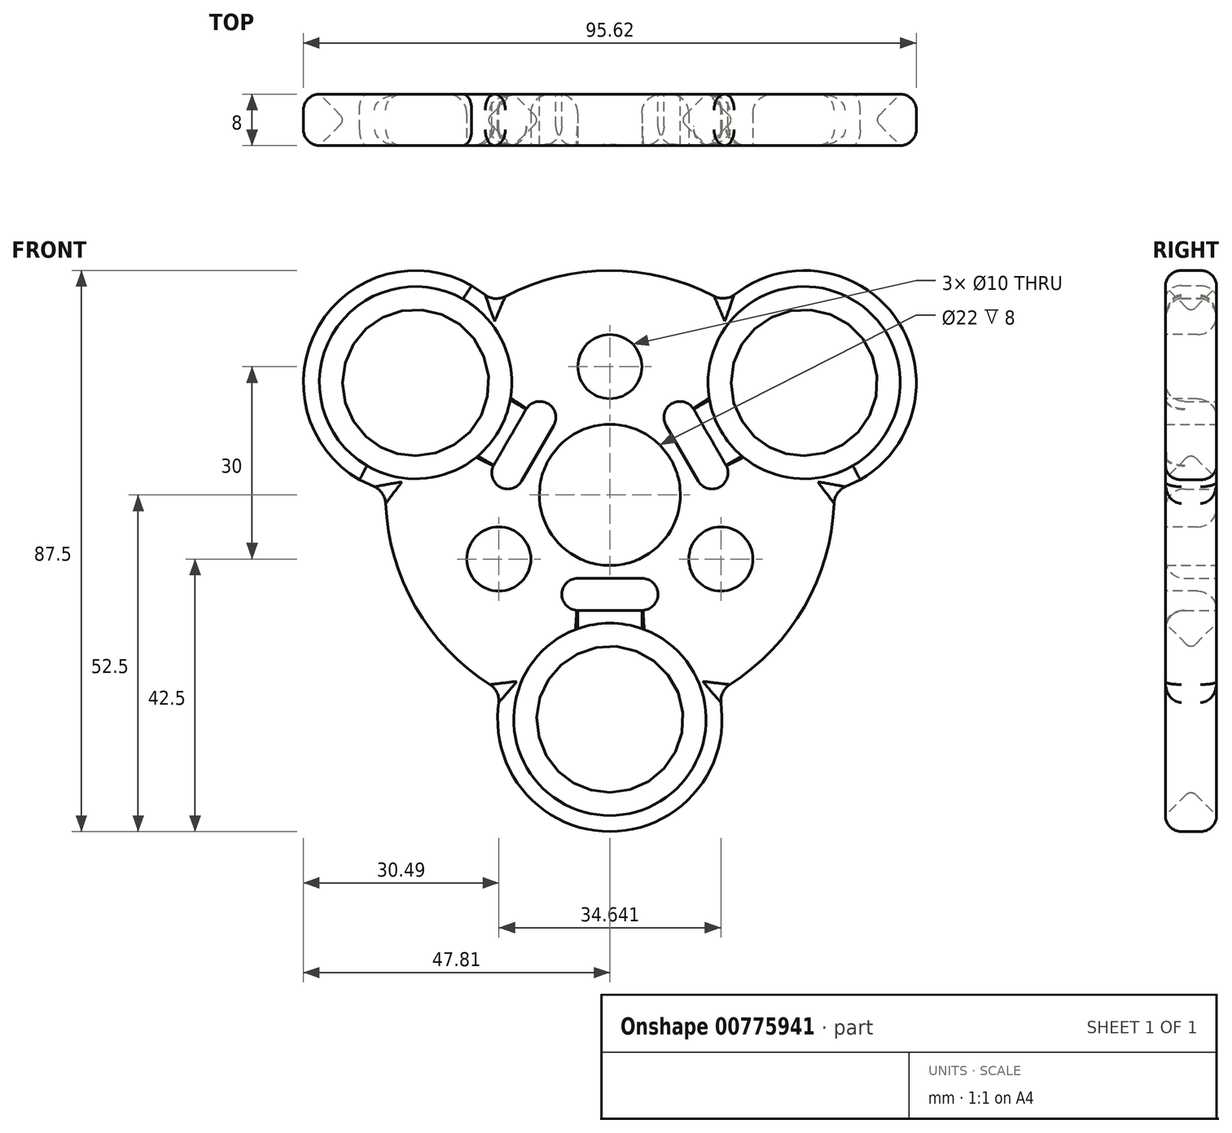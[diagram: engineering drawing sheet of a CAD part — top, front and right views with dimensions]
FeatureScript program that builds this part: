
annotation { "Feature Type Name" : "Feature", "Feature Type Description" : "" }
export const myFeature = defineFeature(function(context is Context, id is Id, definition is map)
    precondition{}
    {
        {
            var Q0;
            Q0=qCreatedBy(makeId("Front.planeOp"),FACE);
            var sketch = newSketch(context, id + "F0", { "sketchPlane" : qUnion([Q0])});
            skCircle(sketch, "E0", {"center": v(0, 0) * mm, "radius": 11 * mm});
            skCircle(sketch, "E1", {"center": v(0, 0) * mm, "radius": 17.5 * mm, "construction": true});
            skLineSegment(sketch, "E2", {"start": v(0, 0) * mm, "end": v(-30.31, 17.5) * mm, "construction": true});
            skLineSegment(sketch, "E3", {"start": v(0, 0) * mm, "end": v(30.31, 17.5) * mm, "construction": true});
            skLineSegment(sketch, "E4", {"start": v(0, 0) * mm, "end": v(0, -35) * mm, "construction": true});
            skCircle(sketch, "E5", {"center": v(-30.31, 17.5) * mm, "radius": 11 * mm});
            skCircle(sketch, "E6", {"center": v(30.31, 17.5) * mm, "radius": 11 * mm});
            skCircle(sketch, "E7", {"center": v(0, -35) * mm, "radius": 11 * mm});
            skArc(sketch, "E8", {"start": v(-19.01, 30.86) * mm, "mid": v(-45.47, 26.25) * mm, "end": v(-36.24, 1.03) * mm});
            skArc(sketch, "E9", {"start": v(36.2, 1.02) * mm, "mid": v(45.84, 25.57) * mm, "end": v(20.2, 31.79) * mm});
            skArc(sketch, "E10", {"start": v(-17.43, -33.4) * mm, "mid": v(0.01, -52.5) * mm, "end": v(17.42, -33.37) * mm});
            skLineSegment(sketch, "E11", {"start": v(-15.16, 8.75) * mm, "end": v(15.16, 8.75) * mm, "construction": true});
            skLineSegment(sketch, "E12", {"start": v(15.16, 8.75) * mm, "end": v(0, -17.5) * mm, "construction": true});
            skLineSegment(sketch, "E13", {"start": v(0, -17.5) * mm, "end": v(-15.16, 8.75) * mm, "construction": true});
            skLineSegment(sketch, "E14", {"start": v(0, 8.75) * mm, "end": v(0, 27.78) * mm, "construction": true});
            skLineSegment(sketch, "E15", {"start": v(7.58, -4.38) * mm, "end": v(29.6, -17.1) * mm, "construction": true});
            skLineSegment(sketch, "E16", {"start": v(-7.58, -4.37) * mm, "end": v(-25.82, -14.9) * mm, "construction": true});
            skLineSegment(sketch, "E17", {"start": v(-43.22, -4.87) * mm, "end": v(-17.4, 39.87) * mm, "construction": true});
            skLineSegment(sketch, "E18", {"start": v(12.19, 48.9) * mm, "end": v(48.44, -13.9) * mm, "construction": true});
            skLineSegment(sketch, "E19", {"start": v(-41.25, -35) * mm, "end": v(41.25, -35) * mm, "construction": true});
            skLineSegment(sketch, "E20", {"start": v(-21.56, 32.66) * mm, "end": v(0, 17.5) * mm});
            skLineSegment(sketch, "E21", {"start": v(0, 17.5) * mm, "end": v(21.52, 32.72) * mm});
            skLineSegment(sketch, "E22", {"start": v(-39.06, 2.34) * mm, "end": v(-15.16, -8.75) * mm});
            skLineSegment(sketch, "E23", {"start": v(-15.16, -8.75) * mm, "end": v(-17.57, -35) * mm});
            skLineSegment(sketch, "E24", {"start": v(39.06, 2.34) * mm, "end": v(15.12, -8.73) * mm});
            skLineSegment(sketch, "E25", {"start": v(15.12, -8.73) * mm, "end": v(17.58, -35) * mm});
            skSolve(sketch);
        }
        {
            var Q0;
            Q0=makeQuery(id+"F0.imprint","IMPRINT",FACE,{"disambiguationData":[TD([[makeQuery(id+"F0.imprint","IMPRINT",EDGE,{"derivedFrom":sQuery(id+"F0.wireOp",EDGE,"E0")}),-1.0]])]});
            extrude(context, id + "F1", {"entities" : qUnion([Q0]), "depth" : 8 * mm, "offsetDistance" : 25 * mm});
        }
        {
            var Q0;
            Q0=makeQuery(id+"F1.opExtrude","SWEPT_EDGE",EDGE,{"disambiguationData":[OSD([sQuery(id+"F0.wireOp",EDGE,"E24"),sQuery(id+"F0.wireOp",EDGE,"E25")])]});
            var Q1;
            Q1=makeQuery(id+"F1.opExtrude","SWEPT_EDGE",EDGE,{"disambiguationData":[OSD([sQuery(id+"F0.wireOp",EDGE,"E22"),sQuery(id+"F0.wireOp",EDGE,"E23")])]});
            var Q2;
            Q2=makeQuery(id+"F1.opExtrude","SWEPT_EDGE",EDGE,{"disambiguationData":[OSD([sQuery(id+"F0.wireOp",EDGE,"E20"),sQuery(id+"F0.wireOp",EDGE,"E21")])]});
            fillet(context, id + "F2", {"entities" : qUnion([Q0, Q1, Q2]), "radius" : 10 * mm, "tangentPropagation" : true, "allowEdgeOverflow" : false});
        }
        {
            var Q0;
            Q0=qCreatedBy(makeId("Front.planeOp"),FACE);
            var sketch = newSketch(context, id + "F3", { "sketchPlane" : qUnion([Q0])});
            skArc(sketch, "E26", {"start": v(10.86, -33.27) * mm, "mid": v(30.31, -17.5) * mm, "end": v(34.25, 7.23) * mm});
            skCircle(sketch, "E27.0", {"center": v(0, 0) * mm, "radius": 11 * mm});
            skCircle(sketch, "E28.0", {"center": v(30.31, 17.5) * mm, "radius": 11 * mm});
            skCircle(sketch, "E29.0", {"center": v(-30.31, 17.5) * mm, "radius": 11 * mm});
            skCircle(sketch, "E30.0", {"center": v(0, -35) * mm, "radius": 11 * mm});
            skArc(sketch, "E31.trimOffspring", {"start": v(23.38, 26.04) * mm, "mid": v(0, 35) * mm, "end": v(-23.38, 26.04) * mm});
            skArc(sketch, "E32.trimOffspring", {"start": v(-34.25, 7.23) * mm, "mid": v(-30.31, -17.5) * mm, "end": v(-10.86, -33.27) * mm});
            skSolve(sketch);
        }
        {
            var Q0;
            {var subQ1=sQuery(id+"F3.wireOp",EDGE,"E26");Q0=makeQuery(id+"F3.imprint","IMPRINT",FACE,{"disambiguationData":[TD([[makeQuery(id+"F3.imprint","IMPRINT",EDGE,{"derivedFrom":subQ1}),1.0]])]});}
            var Q1;
            Q1=makeQuery(id+"F1.opExtrude","CAP_FACE",FACE,{"disambiguationData":[OSD([sQuery(id+"F0.wireOp",EDGE,"E0"),sQuery(id+"F0.wireOp",EDGE,"E5"),sQuery(id+"F0.wireOp",EDGE,"E6"),sQuery(id+"F0.wireOp",EDGE,"E7"),sQuery(id+"F0.wireOp",EDGE,"E8"),sQuery(id+"F0.wireOp",EDGE,"E9"),sQuery(id+"F0.wireOp",EDGE,"E10"),sQuery(id+"F0.wireOp",EDGE,"E20"),sQuery(id+"F0.wireOp",EDGE,"E21"),sQuery(id+"F0.wireOp",EDGE,"E22"),sQuery(id+"F0.wireOp",EDGE,"E23"),sQuery(id+"F0.wireOp",EDGE,"E24"),sQuery(id+"F0.wireOp",EDGE,"E25")])],"isStart":false});
            extrude(context, id + "F4", {"entities" : qUnion([Q0]), "operationType" : NewBodyOperationType.ADD, "endBound" : BoundingType.UP_TO_SURFACE, "depth" : 7 * mm, "endBoundEntityFace" : qUnion([Q1]), "offsetDistance" : 25 * mm});
        }
        {
            var Q0;
            Q0=makeQuery(id+"F4.opExtrude","CAP_EDGE",EDGE,{"disambiguationData":[OSD([sQuery(id+"F3.wireOp",EDGE,"E32.trimOffspring")])],"isStart":false});
            var Q1;
            Q1=makeQuery(id+"F1.opExtrude","CAP_EDGE",EDGE,{"disambiguationData":[OSD([sQuery(id+"F0.wireOp",EDGE,"E10")])],"isStart":false});
            var Q2;
            Q2=makeQuery(id+"F4.opExtrude","CAP_EDGE",EDGE,{"disambiguationData":[OSD([sQuery(id+"F3.wireOp",EDGE,"E26")])],"isStart":false});
            var Q3;
            Q3=makeQuery(id+"F1.opExtrude","CAP_EDGE",EDGE,{"disambiguationData":[OSD([sQuery(id+"F0.wireOp",EDGE,"E9")])],"isStart":false});
            var Q4;
            Q4=makeQuery(id+"F4.opExtrude","CAP_EDGE",EDGE,{"disambiguationData":[OSD([sQuery(id+"F3.wireOp",EDGE,"E31.trimOffspring")])],"isStart":false});
            var Q5;
            Q5=makeQuery(id+"F1.opExtrude","CAP_EDGE",EDGE,{"disambiguationData":[OSD([sQuery(id+"F0.wireOp",EDGE,"E8")])],"isStart":false});
            var Q6;
            Q6=makeQuery(id+"F1.opExtrude","CAP_EDGE",EDGE,{"disambiguationData":[OSD([sQuery(id+"F0.wireOp",EDGE,"E20")])],"isStart":false});
            var Q7;
            Q7=makeQuery(id+"F1.opExtrude","CAP_EDGE",EDGE,{"disambiguationData":[OSD([sQuery(id+"F0.wireOp",EDGE,"E22")])],"isStart":false});
            var Q8;
            Q8=makeQuery(id+"F1.opExtrude","CAP_EDGE",EDGE,{"disambiguationData":[OSD([sQuery(id+"F0.wireOp",EDGE,"E21")])],"isStart":false});
            var Q9;
            Q9=makeQuery(id+"F1.opExtrude","CAP_EDGE",EDGE,{"disambiguationData":[OSD([sQuery(id+"F0.wireOp",EDGE,"E24")])],"isStart":false});
            var Q10;
            Q10=makeQuery(id+"F4.opExtrude","CAP_EDGE",EDGE,{"disambiguationData":[OSD([sQuery(id+"F3.wireOp",EDGE,"E32.trimOffspring")])],"isStart":true});
            var Q11;
            Q11=makeQuery(id+"F1.opExtrude","CAP_EDGE",EDGE,{"disambiguationData":[OSD([sQuery(id+"F0.wireOp",EDGE,"E10")])],"isStart":true});
            var Q12;
            Q12=makeQuery(id+"F1.opExtrude","CAP_EDGE",EDGE,{"disambiguationData":[OSD([sQuery(id+"F0.wireOp",EDGE,"E23")])],"isStart":true});
            var Q13;
            Q13=makeQuery(id+"F1.opExtrude","CAP_EDGE",EDGE,{"disambiguationData":[OSD([sQuery(id+"F0.wireOp",EDGE,"E25")])],"isStart":true});
            var Q14;
            Q14=makeQuery(id+"F4.opExtrude","CAP_EDGE",EDGE,{"disambiguationData":[OSD([sQuery(id+"F3.wireOp",EDGE,"E26")])],"isStart":true});
            var Q15;
            Q15=makeQuery(id+"F1.opExtrude","CAP_EDGE",EDGE,{"disambiguationData":[OSD([sQuery(id+"F0.wireOp",EDGE,"E24")])],"isStart":true});
            var Q16;
            Q16=makeQuery(id+"F1.opExtrude","CAP_EDGE",EDGE,{"disambiguationData":[OSD([sQuery(id+"F0.wireOp",EDGE,"E9")])],"isStart":true});
            var Q17;
            Q17=makeQuery(id+"F1.opExtrude","CAP_EDGE",EDGE,{"disambiguationData":[OSD([sQuery(id+"F0.wireOp",EDGE,"E21")])],"isStart":true});
            var Q18;
            Q18=makeQuery(id+"F4.opExtrude","CAP_EDGE",EDGE,{"disambiguationData":[OSD([sQuery(id+"F3.wireOp",EDGE,"E31.trimOffspring")])],"isStart":true});
            var Q19;
            Q19=makeQuery(id+"F1.opExtrude","CAP_EDGE",EDGE,{"disambiguationData":[OSD([sQuery(id+"F0.wireOp",EDGE,"E20")])],"isStart":true});
            var Q20;
            Q20=makeQuery(id+"F1.opExtrude","CAP_EDGE",EDGE,{"disambiguationData":[OSD([sQuery(id+"F0.wireOp",EDGE,"E8")])],"isStart":true});
            var Q21;
            Q21=makeQuery(id+"F1.opExtrude","CAP_EDGE",EDGE,{"disambiguationData":[OSD([sQuery(id+"F0.wireOp",EDGE,"E22")])],"isStart":true});
            var Q22;
            Q22=makeQuery(id+"F4.opExtrude","TWEAK_EDGE",EDGE,{"derivedFrom":[makeQuery(id+"F1.opExtrude","CAP_FACE",FACE,{"disambiguationData":[OSD([sQuery(id+"F0.wireOp",EDGE,"E0"),sQuery(id+"F0.wireOp",EDGE,"E5"),sQuery(id+"F0.wireOp",EDGE,"E6"),sQuery(id+"F0.wireOp",EDGE,"E7"),sQuery(id+"F0.wireOp",EDGE,"E8"),sQuery(id+"F0.wireOp",EDGE,"E9"),sQuery(id+"F0.wireOp",EDGE,"E10"),sQuery(id+"F0.wireOp",EDGE,"E20"),sQuery(id+"F0.wireOp",EDGE,"E21"),sQuery(id+"F0.wireOp",EDGE,"E22"),sQuery(id+"F0.wireOp",EDGE,"E23"),sQuery(id+"F0.wireOp",EDGE,"E24"),sQuery(id+"F0.wireOp",EDGE,"E25")])],"isStart":false}),makeQuery(id+"F3.imprint","IMPRINT",EDGE,{"derivedFrom":sQuery(id+"F3.wireOp",EDGE,"E32.trimOffspring")})]});
            var Q23;
            Q23=makeQuery(id+"F4.opExtrude","TWEAK_EDGE",EDGE,{"derivedFrom":[makeQuery(id+"F1.opExtrude","CAP_FACE",FACE,{"disambiguationData":[OSD([sQuery(id+"F0.wireOp",EDGE,"E0"),sQuery(id+"F0.wireOp",EDGE,"E5"),sQuery(id+"F0.wireOp",EDGE,"E6"),sQuery(id+"F0.wireOp",EDGE,"E7"),sQuery(id+"F0.wireOp",EDGE,"E8"),sQuery(id+"F0.wireOp",EDGE,"E9"),sQuery(id+"F0.wireOp",EDGE,"E10"),sQuery(id+"F0.wireOp",EDGE,"E20"),sQuery(id+"F0.wireOp",EDGE,"E21"),sQuery(id+"F0.wireOp",EDGE,"E22"),sQuery(id+"F0.wireOp",EDGE,"E23"),sQuery(id+"F0.wireOp",EDGE,"E24"),sQuery(id+"F0.wireOp",EDGE,"E25")])],"isStart":false}),makeQuery(id+"F3.imprint","IMPRINT",EDGE,{"derivedFrom":sQuery(id+"F3.wireOp",EDGE,"E31.trimOffspring")})]});
            var Q24;
            Q24=makeQuery(id+"F4.opExtrude","TWEAK_EDGE",EDGE,{"derivedFrom":[makeQuery(id+"F1.opExtrude","CAP_FACE",FACE,{"disambiguationData":[OSD([sQuery(id+"F0.wireOp",EDGE,"E0"),sQuery(id+"F0.wireOp",EDGE,"E5"),sQuery(id+"F0.wireOp",EDGE,"E6"),sQuery(id+"F0.wireOp",EDGE,"E7"),sQuery(id+"F0.wireOp",EDGE,"E8"),sQuery(id+"F0.wireOp",EDGE,"E9"),sQuery(id+"F0.wireOp",EDGE,"E10"),sQuery(id+"F0.wireOp",EDGE,"E20"),sQuery(id+"F0.wireOp",EDGE,"E21"),sQuery(id+"F0.wireOp",EDGE,"E22"),sQuery(id+"F0.wireOp",EDGE,"E23"),sQuery(id+"F0.wireOp",EDGE,"E24"),sQuery(id+"F0.wireOp",EDGE,"E25")])],"isStart":false}),makeQuery(id+"F3.imprint","IMPRINT",EDGE,{"derivedFrom":sQuery(id+"F3.wireOp",EDGE,"E26")})]});
            var Q25;
            Q25=makeQuery(id+"F1.opExtrude","CAP_EDGE",EDGE,{"disambiguationData":[OSD([sQuery(id+"F0.wireOp",EDGE,"E25")])],"isStart":false});
            var Q26;
            Q26=makeQuery(id+"F1.opExtrude","CAP_EDGE",EDGE,{"disambiguationData":[OSD([sQuery(id+"F0.wireOp",EDGE,"E23")])],"isStart":false});
            fillet(context, id + "F5", {"entities" : qUnion([Q0, Q1, Q2, Q3, Q4, Q5, Q6, Q7, Q8, Q9, Q10, Q11, Q12, Q13, Q14, Q15, Q16, Q17, Q18, Q19, Q20, Q21, Q22, Q23, Q24, Q25, Q26]), "radius" : 2.5 * mm, "tangentPropagation" : true, "allowEdgeOverflow" : false});
        }
        {
            var Q0;
            Q0=makeQuery(id+"F4.boolean.opBoolean","MERGE",FACE,{"derivedFrom":[makeQuery(id+"F1.opExtrude","CAP_FACE",FACE,{"disambiguationData":[OSD([sQuery(id+"F0.wireOp",EDGE,"E0"),sQuery(id+"F0.wireOp",EDGE,"E5"),sQuery(id+"F0.wireOp",EDGE,"E6"),sQuery(id+"F0.wireOp",EDGE,"E7"),sQuery(id+"F0.wireOp",EDGE,"E8"),sQuery(id+"F0.wireOp",EDGE,"E9"),sQuery(id+"F0.wireOp",EDGE,"E10"),sQuery(id+"F0.wireOp",EDGE,"E20"),sQuery(id+"F0.wireOp",EDGE,"E21"),sQuery(id+"F0.wireOp",EDGE,"E22"),sQuery(id+"F0.wireOp",EDGE,"E23"),sQuery(id+"F0.wireOp",EDGE,"E24"),sQuery(id+"F0.wireOp",EDGE,"E25")])],"isStart":false}),makeQuery(id+"F4.opExtrude","CAP_FACE",FACE,{"disambiguationData":[OSD([sQuery(id+"F3.wireOp",EDGE,"E26"),sQuery(id+"F3.wireOp",EDGE,"E27.0"),sQuery(id+"F3.wireOp",EDGE,"E28.0"),sQuery(id+"F3.wireOp",EDGE,"E29.0"),sQuery(id+"F3.wireOp",EDGE,"E30.0"),sQuery(id+"F3.wireOp",EDGE,"E31.trimOffspring"),sQuery(id+"F3.wireOp",EDGE,"E32.trimOffspring")])],"isStart":false})]});
            var sketch = newSketch(context, id + "F6", { "sketchPlane" : qUnion([Q0])});
            skCircle(sketch, "E33", {"center": v(-17.32, -10) * mm, "radius": 5 * mm});
            skCircle(sketch, "E34", {"center": v(0, 20) * mm, "radius": 5 * mm});
            skCircle(sketch, "E35", {"center": v(17.32, -10) * mm, "radius": 5 * mm});
            skLineSegment(sketch, "E36", {"start": v(0, 0) * mm, "end": v(-17.32, -10) * mm, "construction": true});
            skLineSegment(sketch, "E37", {"start": v(0, 0) * mm, "end": v(0, 20) * mm, "construction": true});
            skLineSegment(sketch, "E38", {"start": v(0, 0) * mm, "end": v(17.32, -10) * mm, "construction": true});
            skSolve(sketch);
        }
        {
            var Q0;
            Q0=makeQuery(id+"F6.imprint","IMPRINT",FACE,{"disambiguationData":[TD([[makeQuery(id+"F6.imprint","IMPRINT",EDGE,{"derivedFrom":sQuery(id+"F6.wireOp",EDGE,"E35")}),1.0]])]});
            var Q1;
            Q1=makeQuery(id+"F6.imprint","IMPRINT",FACE,{"disambiguationData":[TD([[makeQuery(id+"F6.imprint","IMPRINT",EDGE,{"derivedFrom":sQuery(id+"F6.wireOp",EDGE,"E33")}),1.0]])]});
            var Q2;
            Q2=makeQuery(id+"F6.imprint","IMPRINT",FACE,{"disambiguationData":[TD([[makeQuery(id+"F6.imprint","IMPRINT",EDGE,{"derivedFrom":sQuery(id+"F6.wireOp",EDGE,"E34")}),1.0]])]});
            extrude(context, id + "F7", {"entities" : qUnion([Q0, Q1, Q2]), "operationType" : NewBodyOperationType.REMOVE, "oppositeDirection" : true, "depth" : 25 * mm, "offsetDistance" : 25 * mm});
        }
        {
            var Q0;
            Q0=makeQuery(id+"F7.boolean.opBoolean","COPY",EDGE,{"derivedFrom":makeQuery(id+"F7.opExtrude","CAP_EDGE",EDGE,{"disambiguationData":[OSD([sQuery(id+"F6.wireOp",EDGE,"E33")])],"isStart":true})});
            var Q1;
            Q1=makeQuery(id+"F7.boolean.opBoolean","COPY",EDGE,{"derivedFrom":makeQuery(id+"F7.opExtrude","CAP_EDGE",EDGE,{"disambiguationData":[OSD([sQuery(id+"F6.wireOp",EDGE,"E34")])],"isStart":true})});
            var Q2;
            Q2=makeQuery(id+"F7.boolean.opBoolean","COPY",EDGE,{"derivedFrom":makeQuery(id+"F7.opExtrude","CAP_EDGE",EDGE,{"disambiguationData":[OSD([sQuery(id+"F6.wireOp",EDGE,"E35")])],"isStart":true})});
            var Q3;
            Q3=makeQuery(id+"F7.boolean.opBoolean","INTERSECT",EDGE,{"derivedFrom":[makeQuery(id+"F4.boolean.opBoolean","MERGE",FACE,{"derivedFrom":[makeQuery(id+"F1.opExtrude","CAP_FACE",FACE,{"disambiguationData":[OSD([sQuery(id+"F0.wireOp",EDGE,"E0"),sQuery(id+"F0.wireOp",EDGE,"E5"),sQuery(id+"F0.wireOp",EDGE,"E6"),sQuery(id+"F0.wireOp",EDGE,"E7"),sQuery(id+"F0.wireOp",EDGE,"E8"),sQuery(id+"F0.wireOp",EDGE,"E9"),sQuery(id+"F0.wireOp",EDGE,"E10"),sQuery(id+"F0.wireOp",EDGE,"E20"),sQuery(id+"F0.wireOp",EDGE,"E21"),sQuery(id+"F0.wireOp",EDGE,"E22"),sQuery(id+"F0.wireOp",EDGE,"E23"),sQuery(id+"F0.wireOp",EDGE,"E24"),sQuery(id+"F0.wireOp",EDGE,"E25")])],"isStart":true}),makeQuery(id+"F4.opExtrude","CAP_FACE",FACE,{"disambiguationData":[OSD([sQuery(id+"F3.wireOp",EDGE,"E26"),sQuery(id+"F3.wireOp",EDGE,"E27.0"),sQuery(id+"F3.wireOp",EDGE,"E28.0"),sQuery(id+"F3.wireOp",EDGE,"E29.0"),sQuery(id+"F3.wireOp",EDGE,"E30.0"),sQuery(id+"F3.wireOp",EDGE,"E31.trimOffspring"),sQuery(id+"F3.wireOp",EDGE,"E32.trimOffspring")])],"isStart":true})]}),makeQuery(id+"F7.opExtrude","SWEPT_FACE",FACE,{"disambiguationData":[OSD([sQuery(id+"F6.wireOp",EDGE,"E35")])]})]});
            var Q4;
            Q4=makeQuery(id+"F7.boolean.opBoolean","INTERSECT",EDGE,{"derivedFrom":[makeQuery(id+"F4.boolean.opBoolean","MERGE",FACE,{"derivedFrom":[makeQuery(id+"F1.opExtrude","CAP_FACE",FACE,{"disambiguationData":[OSD([sQuery(id+"F0.wireOp",EDGE,"E0"),sQuery(id+"F0.wireOp",EDGE,"E5"),sQuery(id+"F0.wireOp",EDGE,"E6"),sQuery(id+"F0.wireOp",EDGE,"E7"),sQuery(id+"F0.wireOp",EDGE,"E8"),sQuery(id+"F0.wireOp",EDGE,"E9"),sQuery(id+"F0.wireOp",EDGE,"E10"),sQuery(id+"F0.wireOp",EDGE,"E20"),sQuery(id+"F0.wireOp",EDGE,"E21"),sQuery(id+"F0.wireOp",EDGE,"E22"),sQuery(id+"F0.wireOp",EDGE,"E23"),sQuery(id+"F0.wireOp",EDGE,"E24"),sQuery(id+"F0.wireOp",EDGE,"E25")])],"isStart":true}),makeQuery(id+"F4.opExtrude","CAP_FACE",FACE,{"disambiguationData":[OSD([sQuery(id+"F3.wireOp",EDGE,"E26"),sQuery(id+"F3.wireOp",EDGE,"E27.0"),sQuery(id+"F3.wireOp",EDGE,"E28.0"),sQuery(id+"F3.wireOp",EDGE,"E29.0"),sQuery(id+"F3.wireOp",EDGE,"E30.0"),sQuery(id+"F3.wireOp",EDGE,"E31.trimOffspring"),sQuery(id+"F3.wireOp",EDGE,"E32.trimOffspring")])],"isStart":true})]}),makeQuery(id+"F7.opExtrude","SWEPT_FACE",FACE,{"disambiguationData":[OSD([sQuery(id+"F6.wireOp",EDGE,"E34")])]})]});
            var Q5;
            Q5=makeQuery(id+"F7.boolean.opBoolean","INTERSECT",EDGE,{"derivedFrom":[makeQuery(id+"F4.boolean.opBoolean","MERGE",FACE,{"derivedFrom":[makeQuery(id+"F1.opExtrude","CAP_FACE",FACE,{"disambiguationData":[OSD([sQuery(id+"F0.wireOp",EDGE,"E0"),sQuery(id+"F0.wireOp",EDGE,"E5"),sQuery(id+"F0.wireOp",EDGE,"E6"),sQuery(id+"F0.wireOp",EDGE,"E7"),sQuery(id+"F0.wireOp",EDGE,"E8"),sQuery(id+"F0.wireOp",EDGE,"E9"),sQuery(id+"F0.wireOp",EDGE,"E10"),sQuery(id+"F0.wireOp",EDGE,"E20"),sQuery(id+"F0.wireOp",EDGE,"E21"),sQuery(id+"F0.wireOp",EDGE,"E22"),sQuery(id+"F0.wireOp",EDGE,"E23"),sQuery(id+"F0.wireOp",EDGE,"E24"),sQuery(id+"F0.wireOp",EDGE,"E25")])],"isStart":true}),makeQuery(id+"F4.opExtrude","CAP_FACE",FACE,{"disambiguationData":[OSD([sQuery(id+"F3.wireOp",EDGE,"E26"),sQuery(id+"F3.wireOp",EDGE,"E27.0"),sQuery(id+"F3.wireOp",EDGE,"E28.0"),sQuery(id+"F3.wireOp",EDGE,"E29.0"),sQuery(id+"F3.wireOp",EDGE,"E30.0"),sQuery(id+"F3.wireOp",EDGE,"E31.trimOffspring"),sQuery(id+"F3.wireOp",EDGE,"E32.trimOffspring")])],"isStart":true})]}),makeQuery(id+"F7.opExtrude","SWEPT_FACE",FACE,{"disambiguationData":[OSD([sQuery(id+"F6.wireOp",EDGE,"E33")])]})]});
            fillet(context, id + "F8", {"entities" : qUnion([Q0, Q1, Q2, Q3, Q4, Q5]), "radius" : 3 * mm, "tangentPropagation" : true, "allowEdgeOverflow" : false});
        }
        {
            var Q0;
            Q0=makeQuery(id+"F4.boolean.opBoolean","INTERSECT",EDGE,{"derivedFrom":[makeQuery(id+"F1.opExtrude","SWEPT_FACE",FACE,{"disambiguationData":[OSD([sQuery(id+"F0.wireOp",EDGE,"E23")])]}),makeQuery(id+"F4.opExtrude","SWEPT_FACE",FACE,{"disambiguationData":[OSD([sQuery(id+"F3.wireOp",EDGE,"E32.trimOffspring")])]})]});
            var Q1;
            Q1=makeQuery(id+"F4.boolean.opBoolean","INTERSECT",EDGE,{"derivedFrom":[makeQuery(id+"F1.opExtrude","SWEPT_FACE",FACE,{"disambiguationData":[OSD([sQuery(id+"F0.wireOp",EDGE,"E22")])]}),makeQuery(id+"F4.opExtrude","SWEPT_FACE",FACE,{"disambiguationData":[OSD([sQuery(id+"F3.wireOp",EDGE,"E32.trimOffspring")])]})]});
            var Q2;
            Q2=makeQuery(id+"F4.boolean.opBoolean","INTERSECT",EDGE,{"derivedFrom":[makeQuery(id+"F1.opExtrude","SWEPT_FACE",FACE,{"disambiguationData":[OSD([sQuery(id+"F0.wireOp",EDGE,"E20")])]}),makeQuery(id+"F4.opExtrude","SWEPT_FACE",FACE,{"disambiguationData":[OSD([sQuery(id+"F3.wireOp",EDGE,"E31.trimOffspring")])]})]});
            var Q3;
            Q3=makeQuery(id+"F4.boolean.opBoolean","INTERSECT",EDGE,{"derivedFrom":[makeQuery(id+"F1.opExtrude","SWEPT_FACE",FACE,{"disambiguationData":[OSD([sQuery(id+"F0.wireOp",EDGE,"E21")])]}),makeQuery(id+"F4.opExtrude","SWEPT_FACE",FACE,{"disambiguationData":[OSD([sQuery(id+"F3.wireOp",EDGE,"E31.trimOffspring")])]})]});
            var Q4;
            Q4=makeQuery(id+"F4.boolean.opBoolean","INTERSECT",EDGE,{"derivedFrom":[makeQuery(id+"F1.opExtrude","SWEPT_FACE",FACE,{"disambiguationData":[OSD([sQuery(id+"F0.wireOp",EDGE,"E24")])]}),makeQuery(id+"F4.opExtrude","SWEPT_FACE",FACE,{"disambiguationData":[OSD([sQuery(id+"F3.wireOp",EDGE,"E26")])]})]});
            var Q5;
            Q5=makeQuery(id+"F4.boolean.opBoolean","INTERSECT",EDGE,{"derivedFrom":[makeQuery(id+"F1.opExtrude","SWEPT_FACE",FACE,{"disambiguationData":[OSD([sQuery(id+"F0.wireOp",EDGE,"E25")])]}),makeQuery(id+"F4.opExtrude","SWEPT_FACE",FACE,{"disambiguationData":[OSD([sQuery(id+"F3.wireOp",EDGE,"E26")])]})]});
            fillet(context, id + "F9", {"entities" : qUnion([Q0, Q1, Q2, Q3, Q4, Q5]), "radius" : 3 * mm, "tangentPropagation" : true, "allowEdgeOverflow" : false});
        }
        {
            var Q0;
            Q0=makeQuery(id+"F4.boolean.opBoolean","MERGE",FACE,{"derivedFrom":[makeQuery(id+"F1.opExtrude","CAP_FACE",FACE,{"disambiguationData":[OSD([sQuery(id+"F0.wireOp",EDGE,"E0"),sQuery(id+"F0.wireOp",EDGE,"E5"),sQuery(id+"F0.wireOp",EDGE,"E6"),sQuery(id+"F0.wireOp",EDGE,"E7"),sQuery(id+"F0.wireOp",EDGE,"E8"),sQuery(id+"F0.wireOp",EDGE,"E9"),sQuery(id+"F0.wireOp",EDGE,"E10"),sQuery(id+"F0.wireOp",EDGE,"E20"),sQuery(id+"F0.wireOp",EDGE,"E21"),sQuery(id+"F0.wireOp",EDGE,"E22"),sQuery(id+"F0.wireOp",EDGE,"E23"),sQuery(id+"F0.wireOp",EDGE,"E24"),sQuery(id+"F0.wireOp",EDGE,"E25")])],"isStart":true}),makeQuery(id+"F4.opExtrude","CAP_FACE",FACE,{"disambiguationData":[OSD([sQuery(id+"F3.wireOp",EDGE,"E26"),sQuery(id+"F3.wireOp",EDGE,"E27.0"),sQuery(id+"F3.wireOp",EDGE,"E28.0"),sQuery(id+"F3.wireOp",EDGE,"E29.0"),sQuery(id+"F3.wireOp",EDGE,"E30.0"),sQuery(id+"F3.wireOp",EDGE,"E31.trimOffspring"),sQuery(id+"F3.wireOp",EDGE,"E32.trimOffspring")])],"isStart":true})]});
            var sketch = newSketch(context, id + "F10", { "sketchPlane" : qUnion([Q0])});
            skLineSegment(sketch, "E39", {"start": v(8.76, 10.83) * mm, "end": v(13.76, 2.17) * mm});
            skLineSegment(sketch, "E40", {"start": v(5, -13) * mm, "end": v(-5, -13) * mm});
            skLineSegment(sketch, "E41", {"start": v(-8.76, 10.83) * mm, "end": v(-13.76, 2.17) * mm});
            skLineSegment(sketch, "E42", {"start": v(0, 0) * mm, "end": v(-11.26, 6.5) * mm, "construction": true});
            skLineSegment(sketch, "E43", {"start": v(0, 0) * mm, "end": v(0, -13) * mm, "construction": true});
            skLineSegment(sketch, "E44", {"start": v(0, 0) * mm, "end": v(11.26, 6.5) * mm, "construction": true});
            skLineSegment(sketch, "E45", {"start": v(-9.67, 14.25) * mm, "end": v(-9.67, 14.25) * mm});
            skLineSegment(sketch, "E46", {"start": v(-13.09, 13.33) * mm, "end": v(-18.09, 4.67) * mm});
            skLineSegment(sketch, "E47", {"start": v(-17.17, 1.25) * mm, "end": v(-17.17, 1.25) * mm});
            skLineSegment(sketch, "E48", {"start": v(7.5, -15.5) * mm, "end": v(7.5, -15.5) * mm});
            skLineSegment(sketch, "E49", {"start": v(5, -18) * mm, "end": v(-5, -18) * mm});
            skLineSegment(sketch, "E50", {"start": v(-7.5, -15.5) * mm, "end": v(-7.5, -15.5) * mm});
            skLineSegment(sketch, "E51", {"start": v(9.67, 14.25) * mm, "end": v(9.67, 14.25) * mm});
            skLineSegment(sketch, "E52", {"start": v(13.09, 13.33) * mm, "end": v(18.09, 4.67) * mm});
            skLineSegment(sketch, "E53", {"start": v(17.17, 1.25) * mm, "end": v(17.17, 1.25) * mm});
            skPoint(sketch, "E54.visualSharp", {"position": v(19.34, 2.5) * mm});
            skArc(sketch, "E54.filletArc", {"start": v(17.17, 1.25) * mm, "mid": v(18.34, 2.77) * mm, "end": v(18.09, 4.67) * mm});
            skPoint(sketch, "E55.visualSharp", {"position": v(15, 0) * mm});
            skArc(sketch, "E55.filletArc", {"start": v(13.76, 2.17) * mm, "mid": v(15.28, 1) * mm, "end": v(17.17, 1.25) * mm});
            skPoint(sketch, "E56.visualSharp", {"position": v(7.5, 13) * mm});
            skArc(sketch, "E56.filletArc", {"start": v(9.67, 14.25) * mm, "mid": v(8.5, 12.73) * mm, "end": v(8.76, 10.83) * mm});
            skPoint(sketch, "E57.visualSharp", {"position": v(11.84, 15.5) * mm});
            skArc(sketch, "E57.filletArc", {"start": v(13.09, 13.33) * mm, "mid": v(11.57, 14.5) * mm, "end": v(9.67, 14.25) * mm});
            skPoint(sketch, "E58.visualSharp", {"position": v(7.5, -13) * mm});
            skArc(sketch, "E58.filletArc", {"start": v(7.5, -15.5) * mm, "mid": v(6.77, -13.73) * mm, "end": v(5, -13) * mm});
            skPoint(sketch, "E59.visualSharp", {"position": v(7.5, -18) * mm});
            skArc(sketch, "E59.filletArc", {"start": v(5, -18) * mm, "mid": v(6.77, -17.27) * mm, "end": v(7.5, -15.5) * mm});
            skPoint(sketch, "E60.visualSharp", {"position": v(-7.5, -18) * mm});
            skArc(sketch, "E60.filletArc", {"start": v(-7.5, -15.5) * mm, "mid": v(-6.77, -17.27) * mm, "end": v(-5, -18) * mm});
            skPoint(sketch, "E61.visualSharp", {"position": v(-7.5, -13) * mm});
            skArc(sketch, "E61.filletArc", {"start": v(-5, -13) * mm, "mid": v(-6.77, -13.73) * mm, "end": v(-7.5, -15.5) * mm});
            skPoint(sketch, "E62.visualSharp", {"position": v(-15, 0) * mm});
            skArc(sketch, "E62.filletArc", {"start": v(-17.17, 1.25) * mm, "mid": v(-15.28, 1) * mm, "end": v(-13.76, 2.17) * mm});
            skPoint(sketch, "E63.visualSharp", {"position": v(-19.34, 2.5) * mm});
            skArc(sketch, "E63.filletArc", {"start": v(-18.09, 4.67) * mm, "mid": v(-18.34, 2.77) * mm, "end": v(-17.17, 1.25) * mm});
            skPoint(sketch, "E64.visualSharp", {"position": v(-11.84, 15.5) * mm});
            skArc(sketch, "E64.filletArc", {"start": v(-9.67, 14.25) * mm, "mid": v(-11.57, 14.5) * mm, "end": v(-13.09, 13.33) * mm});
            skPoint(sketch, "E65.visualSharp", {"position": v(-7.5, 13) * mm});
            skArc(sketch, "E65.filletArc", {"start": v(-8.76, 10.83) * mm, "mid": v(-8.5, 12.73) * mm, "end": v(-9.67, 14.25) * mm});
            skSolve(sketch);
        }
        {
            var Q0;
            Q0=makeQuery(id+"F10.imprint","IMPRINT",FACE,{"disambiguationData":[TD([[makeQuery(id+"F10.imprint","IMPRINT",EDGE,{"derivedFrom":sQuery(id+"F10.wireOp",EDGE,"E39")}),1.0]])]});
            var Q1;
            Q1=makeQuery(id+"F10.imprint","IMPRINT",FACE,{"disambiguationData":[TD([[makeQuery(id+"F10.imprint","IMPRINT",EDGE,{"derivedFrom":sQuery(id+"F10.wireOp",EDGE,"E40")}),1.0]])]});
            var Q2;
            Q2=makeQuery(id+"F10.imprint","IMPRINT",FACE,{"disambiguationData":[TD([[makeQuery(id+"F10.imprint","IMPRINT",EDGE,{"derivedFrom":sQuery(id+"F10.wireOp",EDGE,"E41")}),-1.0]])]});
            extrude(context, id + "F11", {"entities" : qUnion([Q0, Q1, Q2]), "operationType" : NewBodyOperationType.REMOVE, "oppositeDirection" : true, "depth" : 25 * mm, "offsetDistance" : 25 * mm});
        }
        {
            var Q0;
            Q0=makeQuery(id+"F1.opExtrude","CAP_EDGE",EDGE,{"disambiguationData":[OSD([sQuery(id+"F0.wireOp",EDGE,"E6")])],"isStart":true});
            var Q1;
            Q1=makeQuery(id+"F1.opExtrude","CAP_EDGE",EDGE,{"disambiguationData":[OSD([sQuery(id+"F0.wireOp",EDGE,"E5")])],"isStart":true});
            var Q2;
            Q2=makeQuery(id+"F1.opExtrude","CAP_EDGE",EDGE,{"disambiguationData":[OSD([sQuery(id+"F0.wireOp",EDGE,"E7")])],"isStart":true});
            chamfer(context, id + "F12", {"entities" : qUnion([Q0, Q1, Q2]), "width" : 4 * mm, "tangentPropagation" : true});
        }
        {
            var Q0;
            Q0=makeQuery(id+"F1.opExtrude","CAP_EDGE",EDGE,{"disambiguationData":[OSD([sQuery(id+"F0.wireOp",EDGE,"E7")])],"isStart":false});
            var Q1;
            Q1=makeQuery(id+"F1.opExtrude","CAP_EDGE",EDGE,{"disambiguationData":[OSD([sQuery(id+"F0.wireOp",EDGE,"E5")])],"isStart":false});
            var Q2;
            Q2=makeQuery(id+"F1.opExtrude","CAP_EDGE",EDGE,{"disambiguationData":[OSD([sQuery(id+"F0.wireOp",EDGE,"E6")])],"isStart":false});
            chamfer(context, id + "F13", {"entities" : qUnion([Q0, Q1, Q2]), "width" : 4 * mm, "tangentPropagation" : true});
        }
        {
            var Q0;
            {var subQ0=sQuery(id+"F0.wireOp",EDGE,"E7");Q0=makeQuery(id+"F13.opChamfer","BLEND_EDGE",EDGE,{"blendedFrom":[makeQuery(id+"F1.opExtrude","CAP_EDGE",EDGE,{"disambiguationData":[OSD([subQ0])],"isStart":false}),makeQuery(id+"F12.opChamfer","BLEND_FACE",FACE,{"disambiguationData":[OSD([subQ0])]})],"blendedInto":[makeQuery(id+"F12.opChamfer","BLEND_FACE",FACE,{"disambiguationData":[OSD([subQ0])]})]});}
            var Q1;
            {var subQ0=sQuery(id+"F0.wireOp",EDGE,"E6");Q1=makeQuery(id+"F13.opChamfer","BLEND_EDGE",EDGE,{"blendedFrom":[makeQuery(id+"F1.opExtrude","CAP_EDGE",EDGE,{"disambiguationData":[OSD([subQ0])],"isStart":false}),makeQuery(id+"F12.opChamfer","BLEND_FACE",FACE,{"disambiguationData":[OSD([subQ0])]})],"blendedInto":[makeQuery(id+"F12.opChamfer","BLEND_FACE",FACE,{"disambiguationData":[OSD([subQ0])]})]});}
            var Q2;
            {var subQ0=sQuery(id+"F0.wireOp",EDGE,"E5");Q2=makeQuery(id+"F13.opChamfer","BLEND_EDGE",EDGE,{"blendedFrom":[makeQuery(id+"F1.opExtrude","CAP_EDGE",EDGE,{"disambiguationData":[OSD([subQ0])],"isStart":false}),makeQuery(id+"F12.opChamfer","BLEND_FACE",FACE,{"disambiguationData":[OSD([subQ0])]})],"blendedInto":[makeQuery(id+"F12.opChamfer","BLEND_FACE",FACE,{"disambiguationData":[OSD([subQ0])]})]});}
            fillet(context, id + "F14", {"entities" : qUnion([Q0, Q1, Q2]), "radius" : 1 * mm, "tangentPropagation" : true, "allowEdgeOverflow" : false});
        }
        {
            var Q0;
            Q0=makeQuery(id+"F11.boolean.opBoolean","COPY",EDGE,{"derivedFrom":makeQuery(id+"F11.opExtrude","CAP_EDGE",EDGE,{"disambiguationData":[OSD([sQuery(id+"F10.wireOp",EDGE,"E49")])],"isStart":true})});
            var Q1;
            Q1=makeQuery(id+"F11.boolean.opBoolean","COPY",EDGE,{"derivedFrom":makeQuery(id+"F11.opExtrude","CAP_EDGE",EDGE,{"disambiguationData":[OSD([sQuery(id+"F10.wireOp",EDGE,"E46")])],"isStart":true})});
            var Q2;
            Q2=makeQuery(id+"F11.boolean.opBoolean","COPY",EDGE,{"derivedFrom":makeQuery(id+"F11.opExtrude","CAP_EDGE",EDGE,{"disambiguationData":[OSD([sQuery(id+"F10.wireOp",EDGE,"E52")])],"isStart":true})});
            var Q3;
            {var subQ0=sQuery(id+"F0.wireOp",EDGE,"E25");var subQ1=sQuery(id+"F0.wireOp",EDGE,"E24");var subQ2=sQuery(id+"F0.wireOp",EDGE,"E23");var subQ3=sQuery(id+"F0.wireOp",EDGE,"E22");var subQ4=sQuery(id+"F0.wireOp",EDGE,"E21");var subQ5=sQuery(id+"F0.wireOp",EDGE,"E20");var subQ6=sQuery(id+"F0.wireOp",EDGE,"E10");var subQ7=sQuery(id+"F0.wireOp",EDGE,"E9");var subQ8=sQuery(id+"F0.wireOp",EDGE,"E8");var subQ9=sQuery(id+"F0.wireOp",EDGE,"E7");var subQ10=sQuery(id+"F0.wireOp",EDGE,"E6");var subQ11=sQuery(id+"F0.wireOp",EDGE,"E5");var subQ12=sQuery(id+"F0.wireOp",EDGE,"E0");Q3=makeQuery(id+"F11.boolean.opBoolean","INTERSECT",EDGE,{"derivedFrom":[makeQuery(id+"F4.boolean.opBoolean","MERGE",FACE,{"derivedFrom":[makeQuery(id+"F1.opExtrude","CAP_FACE",FACE,{"disambiguationData":[OSD([subQ12,subQ11,subQ10,subQ9,subQ8,subQ7,subQ6,subQ5,subQ4,subQ3,subQ2,subQ1,subQ0])],"isStart":false}),makeQuery(id+"F4.opExtrude","CAP_FACE",FACE,{"disambiguationData":[OSD([subQ12,subQ11,subQ10,subQ9,subQ8,subQ7,subQ6,subQ5,subQ4,subQ3,subQ2,subQ1,subQ0])],"isStart":false})]}),makeQuery(id+"F11.opExtrude","SWEPT_FACE",FACE,{"disambiguationData":[OSD([sQuery(id+"F10.wireOp",EDGE,"E52")])]})]});}
            var Q4;
            {var subQ0=sQuery(id+"F0.wireOp",EDGE,"E25");var subQ1=sQuery(id+"F0.wireOp",EDGE,"E24");var subQ2=sQuery(id+"F0.wireOp",EDGE,"E23");var subQ3=sQuery(id+"F0.wireOp",EDGE,"E22");var subQ4=sQuery(id+"F0.wireOp",EDGE,"E21");var subQ5=sQuery(id+"F0.wireOp",EDGE,"E20");var subQ6=sQuery(id+"F0.wireOp",EDGE,"E10");var subQ7=sQuery(id+"F0.wireOp",EDGE,"E9");var subQ8=sQuery(id+"F0.wireOp",EDGE,"E8");var subQ9=sQuery(id+"F0.wireOp",EDGE,"E7");var subQ10=sQuery(id+"F0.wireOp",EDGE,"E6");var subQ11=sQuery(id+"F0.wireOp",EDGE,"E5");var subQ12=sQuery(id+"F0.wireOp",EDGE,"E0");Q4=makeQuery(id+"F11.boolean.opBoolean","INTERSECT",EDGE,{"derivedFrom":[makeQuery(id+"F4.boolean.opBoolean","MERGE",FACE,{"derivedFrom":[makeQuery(id+"F1.opExtrude","CAP_FACE",FACE,{"disambiguationData":[OSD([subQ12,subQ11,subQ10,subQ9,subQ8,subQ7,subQ6,subQ5,subQ4,subQ3,subQ2,subQ1,subQ0])],"isStart":false}),makeQuery(id+"F4.opExtrude","CAP_FACE",FACE,{"disambiguationData":[OSD([subQ12,subQ11,subQ10,subQ9,subQ8,subQ7,subQ6,subQ5,subQ4,subQ3,subQ2,subQ1,subQ0])],"isStart":false})]}),makeQuery(id+"F11.opExtrude","SWEPT_FACE",FACE,{"disambiguationData":[OSD([sQuery(id+"F10.wireOp",EDGE,"E46")])]})]});}
            var Q5;
            {var subQ0=sQuery(id+"F0.wireOp",EDGE,"E25");var subQ1=sQuery(id+"F0.wireOp",EDGE,"E24");var subQ2=sQuery(id+"F0.wireOp",EDGE,"E23");var subQ3=sQuery(id+"F0.wireOp",EDGE,"E22");var subQ4=sQuery(id+"F0.wireOp",EDGE,"E21");var subQ5=sQuery(id+"F0.wireOp",EDGE,"E20");var subQ6=sQuery(id+"F0.wireOp",EDGE,"E10");var subQ7=sQuery(id+"F0.wireOp",EDGE,"E9");var subQ8=sQuery(id+"F0.wireOp",EDGE,"E8");var subQ9=sQuery(id+"F0.wireOp",EDGE,"E7");var subQ10=sQuery(id+"F0.wireOp",EDGE,"E6");var subQ11=sQuery(id+"F0.wireOp",EDGE,"E5");var subQ12=sQuery(id+"F0.wireOp",EDGE,"E0");Q5=makeQuery(id+"F11.boolean.opBoolean","INTERSECT",EDGE,{"derivedFrom":[makeQuery(id+"F4.boolean.opBoolean","MERGE",FACE,{"derivedFrom":[makeQuery(id+"F1.opExtrude","CAP_FACE",FACE,{"disambiguationData":[OSD([subQ12,subQ11,subQ10,subQ9,subQ8,subQ7,subQ6,subQ5,subQ4,subQ3,subQ2,subQ1,subQ0])],"isStart":false}),makeQuery(id+"F4.opExtrude","CAP_FACE",FACE,{"disambiguationData":[OSD([subQ12,subQ11,subQ10,subQ9,subQ8,subQ7,subQ6,subQ5,subQ4,subQ3,subQ2,subQ1,subQ0])],"isStart":false})]}),makeQuery(id+"F11.opExtrude","SWEPT_FACE",FACE,{"disambiguationData":[OSD([sQuery(id+"F10.wireOp",EDGE,"E49")])]})]});}
            fillet(context, id + "F15", {"entities" : qUnion([Q0, Q1, Q2, Q3, Q4, Q5]), "radius" : 3 * mm, "tangentPropagation" : true, "allowEdgeOverflow" : false});
        }
    });
